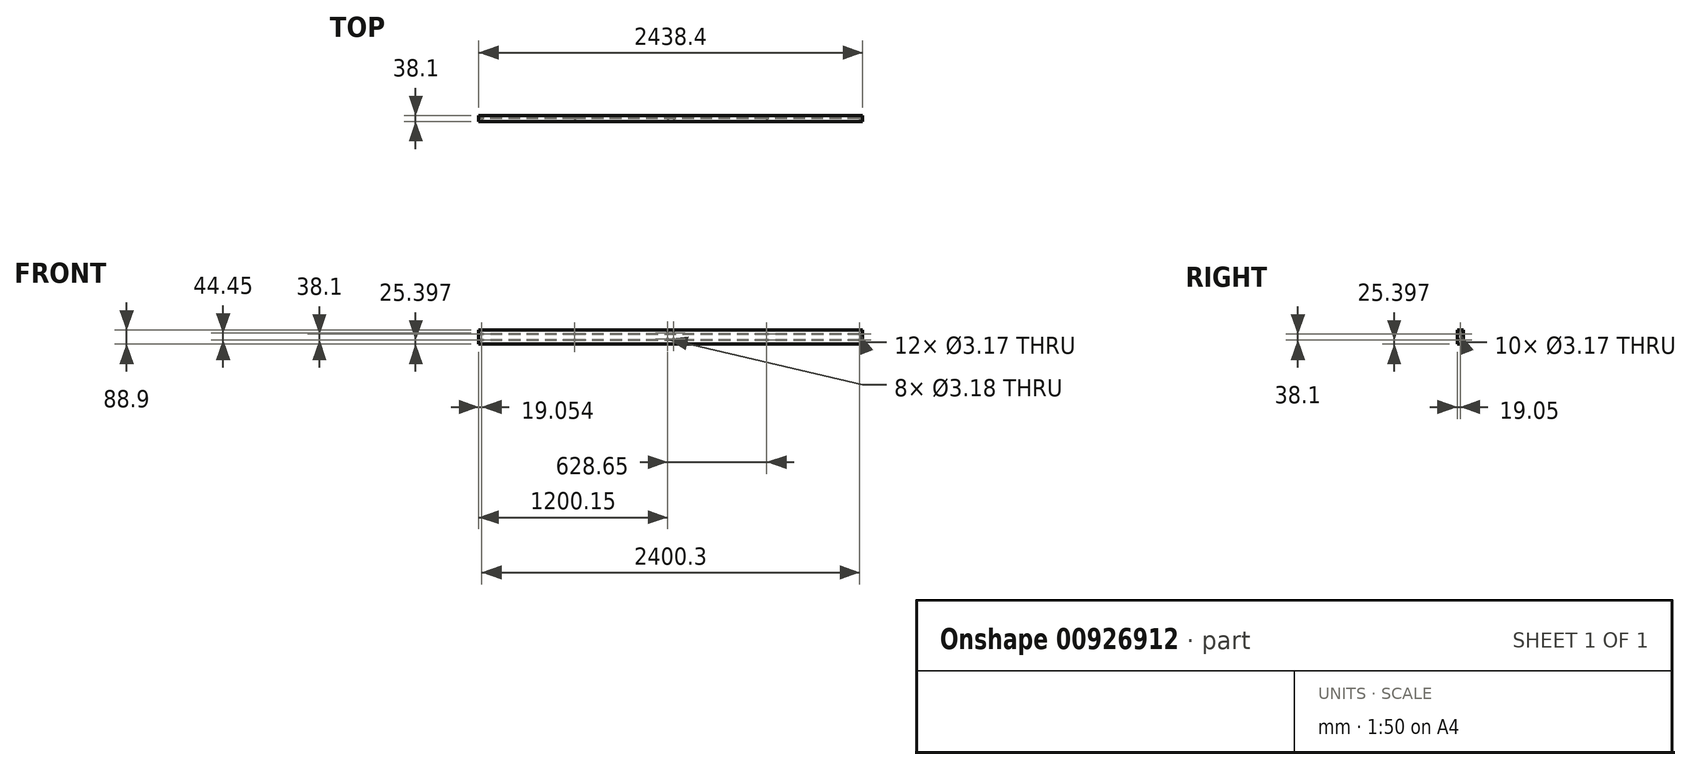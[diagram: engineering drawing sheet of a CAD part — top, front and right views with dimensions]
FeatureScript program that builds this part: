
annotation { "Feature Type Name" : "Feature", "Feature Type Description" : "" }
export const myFeature = defineFeature(function(context is Context, id is Id, definition is map)
    precondition{}
    {
        {
            var Q0;
            Q0=qCreatedBy(makeId("Front.planeOp"),FACE);
            var sketch = newSketch(context, id + "F0", { "sketchPlane" : qUnion([Q0])});
            skLineSegment(sketch, "E0.bottom", {"start": v(-112.7, 108.74) * mm, "end": v(2325.7, 108.74) * mm});
            skLineSegment(sketch, "E0.top", {"start": v(-112.7, 19.84) * mm, "end": v(2325.7, 19.84) * mm});
            skLineSegment(sketch, "E0.left", {"start": v(-112.7, 108.74) * mm, "end": v(-112.7, 19.84) * mm});
            skLineSegment(sketch, "E0.right", {"start": v(2325.7, 108.74) * mm, "end": v(2325.7, 19.84) * mm});
            skSolve(sketch);
        }
        {
            var Q0;
            Q0=makeQuery(id+"F0.imprint","IMPRINT",FACE,{"disambiguationData":[TD([[makeQuery(id+"F0.imprint","IMPRINT",EDGE,{"derivedFrom":sQuery(id+"F0.wireOp",EDGE,"E0.bottom")}),-1.0]])]});
            extrude(context, id + "F1", {"entities" : qUnion([Q0]), "depth" : 38.1 * mm, "offsetDistance" : 25.4 * mm});
        }
        {
            var Q0;
            Q0=makeQuery(id+"F1.opExtrude","CAP_FACE",FACE,{"disambiguationData":[OSD([sQuery(id+"F0.wireOp",EDGE,"E0.bottom"),sQuery(id+"F0.wireOp",EDGE,"E0.top"),sQuery(id+"F0.wireOp",EDGE,"E0.left"),sQuery(id+"F0.wireOp",EDGE,"E0.right")])],"isStart":false});
            var sketch = newSketch(context, id + "F2", { "sketchPlane" : qUnion([Q0])});
            skLineSegment(sketch, "E1", {"start": v(-93.66, 19.84) * mm, "end": v(-93.66, 108.74) * mm, "construction": true});
            skPoint(sketch, "E2", {"position": v(-93.66, 83.34) * mm});
            skPoint(sketch, "E3", {"position": v(-93.66, 45.24) * mm});
            skLineSegment(sketch, "E4", {"start": v(496.9, 108.74) * mm, "end": v(496.9, 19.84) * mm, "construction": true});
            skPoint(sketch, "E5", {"position": v(496.9, 83.34) * mm});
            skPoint(sketch, "E6", {"position": v(496.9, 45.24) * mm});
            skPoint(sketch, "E7.MirrorP", {"position": v(2306.64, 83.34) * mm});
            skPoint(sketch, "E8.MirrorP", {"position": v(2306.64, 45.24) * mm});
            skPoint(sketch, "E9.MirrorP", {"position": v(1716.1, 83.34) * mm});
            skPoint(sketch, "E10.MirrorP", {"position": v(1716.1, 45.24) * mm});
            skLineSegment(sketch, "E11", {"start": v(1106.5, 108.74) * mm, "end": v(1106.5, 19.84) * mm, "construction": true});
            skPoint(sketch, "E12", {"position": v(1087.44, 89.69) * mm});
            skPoint(sketch, "E13", {"position": v(1125.54, 89.69) * mm});
            skPoint(sketch, "E14", {"position": v(1087.44, 51.59) * mm});
            skPoint(sketch, "E15", {"position": v(1125.54, 51.59) * mm});
            skSolve(sketch);
        }
        {
            var Q0;
            Q0=sQuery(id+"F2.wireOp",VERTEX,"E2");
            var Q1;
            Q1=sQuery(id+"F2.wireOp",VERTEX,"E3");
            var Q2;
            Q2=sQuery(id+"F2.wireOp",VERTEX,"E5");
            var Q3;
            Q3=sQuery(id+"F2.wireOp",VERTEX,"E6");
            var Q4;
            Q4=sQuery(id+"F2.wireOp",VERTEX,"E12");
            var Q5;
            Q5=sQuery(id+"F2.wireOp",VERTEX,"E13");
            var Q6;
            Q6=sQuery(id+"F2.wireOp",VERTEX,"E14");
            var Q7;
            Q7=sQuery(id+"F2.wireOp",VERTEX,"E15");
            var Q8;
            Q8=sQuery(id+"F2.wireOp",VERTEX,"E9.MirrorP");
            var Q9;
            Q9=sQuery(id+"F2.wireOp",VERTEX,"E10.MirrorP");
            var Q10;
            Q10=sQuery(id+"F2.wireOp",VERTEX,"E7.MirrorP");
            var Q11;
            Q11=sQuery(id+"F2.wireOp",VERTEX,"E8.MirrorP");
            var Q12;
            Q12=makeQuery(id+"F1.opExtrude","SWEPT_BODY",BODY,{"disambiguationData":[OSD([sQuery(id+"F0.wireOp",EDGE,"E0.bottom"),sQuery(id+"F0.wireOp",EDGE,"E0.top"),sQuery(id+"F0.wireOp",EDGE,"E0.left"),sQuery(id+"F0.wireOp",EDGE,"E0.right")])]});
            hole(context, id + "F3", {"style" : HoleStyle.SIMPLE, "endStyle" : HoleEndStyle.THROUGH, "holeDiameter" : 3.17 * mm, "majorDiameter" : 6.35 * mm, "isTappedThrough" : true, "tappedDepth" : 12.7 * mm, "tapClearance" : 3, "locations" : qUnion([Q0, Q1, Q2, Q3, Q4, Q5, Q6, Q7, Q8, Q9, Q10, Q11]), "scope" : qUnion([Q12])});
        }
        {
            var Q0;
            Q0=makeQuery(id+"F1.opExtrude","SWEPT_FACE",FACE,{"disambiguationData":[OSD([sQuery(id+"F0.wireOp",EDGE,"E0.left")])]});
            var sketch = newSketch(context, id + "F4", { "sketchPlane" : qUnion([Q0])});
            skLineSegment(sketch, "E16", {"start": v(19.05, 108.74) * mm, "end": v(19.05, 19.84) * mm, "construction": true});
            skPoint(sketch, "E17", {"position": v(19.05, 83.34) * mm});
            skPoint(sketch, "E18", {"position": v(19.05, 45.24) * mm});
            skSolve(sketch);
        }
        {
            var Q0;
            Q0=sQuery(id+"F4.wireOp",VERTEX,"E17");
            var Q1;
            Q1=sQuery(id+"F4.wireOp",VERTEX,"E18");
            var Q2;
            Q2=makeQuery(id+"F1.opExtrude","SWEPT_BODY",BODY,{"disambiguationData":[OSD([sQuery(id+"F0.wireOp",EDGE,"E0.bottom"),sQuery(id+"F0.wireOp",EDGE,"E0.top"),sQuery(id+"F0.wireOp",EDGE,"E0.left"),sQuery(id+"F0.wireOp",EDGE,"E0.right")])]});
            hole(context, id + "F5", {"style" : HoleStyle.SIMPLE, "endStyle" : HoleEndStyle.THROUGH, "holeDiameter" : 3.17 * mm, "majorDiameter" : 6.35 * mm, "isTappedThrough" : true, "tappedDepth" : 12.7 * mm, "tapClearance" : 3, "locations" : qUnion([Q0, Q1]), "scope" : qUnion([Q2])});
        }
    });
